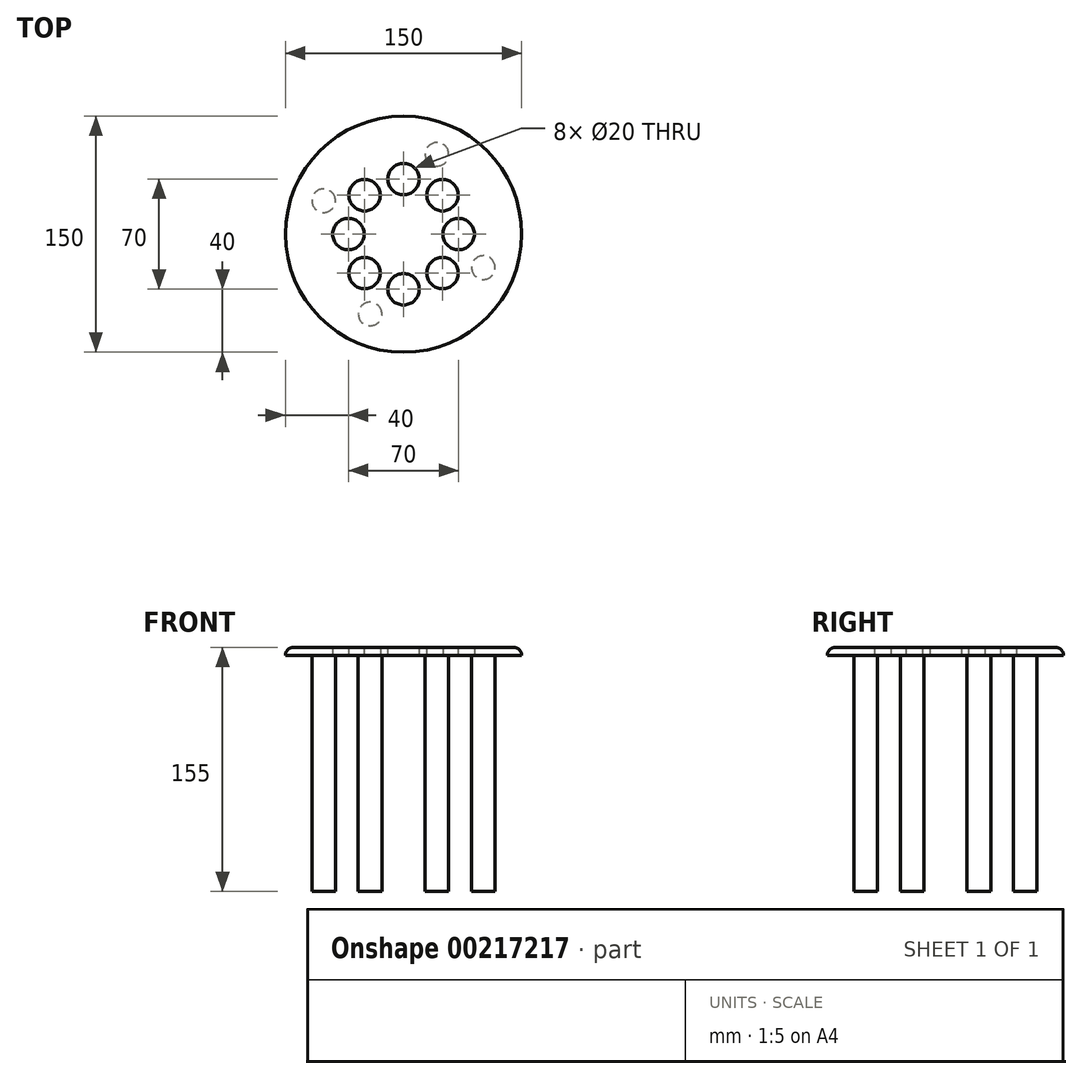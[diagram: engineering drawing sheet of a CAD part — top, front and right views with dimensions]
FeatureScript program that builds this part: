
annotation { "Feature Type Name" : "Feature", "Feature Type Description" : "" }
export const myFeature = defineFeature(function(context is Context, id is Id, definition is map)
    precondition{}
    {
        {
            var Q0;
            Q0=qCreatedBy(makeId("Top.planeOp"),FACE);
            var sketch = newSketch(context, id + "F0", { "sketchPlane" : qUnion([Q0])});
            skCircle(sketch, "E0", {"center": v(0, 0) * mm, "radius": 75 * mm});
            skCircle(sketch, "E1", {"center": v(0, 35) * mm, "radius": 10 * mm});
            skCircle(sketch, "E2.1.0", {"center": v(-24.75, 24.75) * mm, "radius": 10 * mm});
            skCircle(sketch, "E2.2.0", {"center": v(-35, 0) * mm, "radius": 10 * mm});
            skCircle(sketch, "E2.3.0", {"center": v(-24.75, -24.75) * mm, "radius": 10 * mm});
            skCircle(sketch, "E2.4.0", {"center": v(0, -35) * mm, "radius": 10 * mm});
            skCircle(sketch, "E2.5.0", {"center": v(24.75, -24.75) * mm, "radius": 10 * mm});
            skCircle(sketch, "E2.6.0", {"center": v(35, 0) * mm, "radius": 10 * mm});
            skCircle(sketch, "E2.7.0", {"center": v(24.75, 24.75) * mm, "radius": 10 * mm});
            skSolve(sketch);
        }
        {
            var Q0;
            Q0=makeQuery(id+"F0.imprint","IMPRINT",FACE,{"disambiguationData":[TD([[makeQuery(id+"F0.imprint","IMPRINT",EDGE,{"derivedFrom":sQuery(id+"F0.wireOp",EDGE,"E0")}),1.0]])]});
            extrude(context, id + "F1", {"entities" : qUnion([Q0]), "depth" : 5 * mm});
        }
        {
            var Q0;
            Q0=makeQuery(id+"F1.opExtrude","CAP_EDGE",EDGE,{"disambiguationData":[OSD([sQuery(id+"F0.wireOp",EDGE,"E0")])],"isStart":false});
            fillet(context, id + "F2", {"entities" : qUnion([Q0]), "radius" : 5 * mm, "tangentPropagation" : true, "allowEdgeOverflow" : false});
        }
        {
            var Q0;
            Q0=makeQuery(id+"F0.imprint","IMPRINT",FACE,{"disambiguationData":[TD([[makeQuery(id+"F0.imprint","IMPRINT",EDGE,{"derivedFrom":sQuery(id+"F0.wireOp",EDGE,"E0")}),1.0]])]});
            var sketch = newSketch(context, id + "F3", { "sketchPlane" : qUnion([Q0])});
            skCircle(sketch, "E3", {"center": v(50.73, -21.24) * mm, "radius": 7.5 * mm});
            skCircle(sketch, "E4.1.0", {"center": v(21.24, 50.73) * mm, "radius": 7.5 * mm});
            skCircle(sketch, "E4.2.0", {"center": v(-50.73, 21.24) * mm, "radius": 7.5 * mm});
            skCircle(sketch, "E4.3.0", {"center": v(-21.24, -50.73) * mm, "radius": 7.5 * mm});
            skPoint(sketch, "E4.center", {"position": v(0, 0) * mm});
            skSolve(sketch);
        }
        {
            var Q0;
            Q0=makeQuery(id+"F3.imprint","IMPRINT",FACE,{"disambiguationData":[TD([[makeQuery(id+"F3.imprint","IMPRINT",EDGE,{"derivedFrom":sQuery(id+"F3.wireOp",EDGE,"E4.1.0")}),1.0]])]});
            var Q1;
            Q1=makeQuery(id+"F3.imprint","IMPRINT",FACE,{"disambiguationData":[TD([[makeQuery(id+"F3.imprint","IMPRINT",EDGE,{"derivedFrom":sQuery(id+"F3.wireOp",EDGE,"E4.2.0")}),1.0]])]});
            var Q2;
            Q2=makeQuery(id+"F3.imprint","IMPRINT",FACE,{"disambiguationData":[TD([[makeQuery(id+"F3.imprint","IMPRINT",EDGE,{"derivedFrom":sQuery(id+"F3.wireOp",EDGE,"E4.3.0")}),1.0]])]});
            var Q3;
            Q3=makeQuery(id+"F3.imprint","IMPRINT",FACE,{"disambiguationData":[TD([[makeQuery(id+"F3.imprint","IMPRINT",EDGE,{"derivedFrom":sQuery(id+"F3.wireOp",EDGE,"E3")}),1.0]])]});
            extrude(context, id + "F4", {"entities" : qUnion([Q0, Q1, Q2, Q3]), "operationType" : NewBodyOperationType.ADD, "oppositeDirection" : true, "depth" : 150 * mm});
        }
    });
